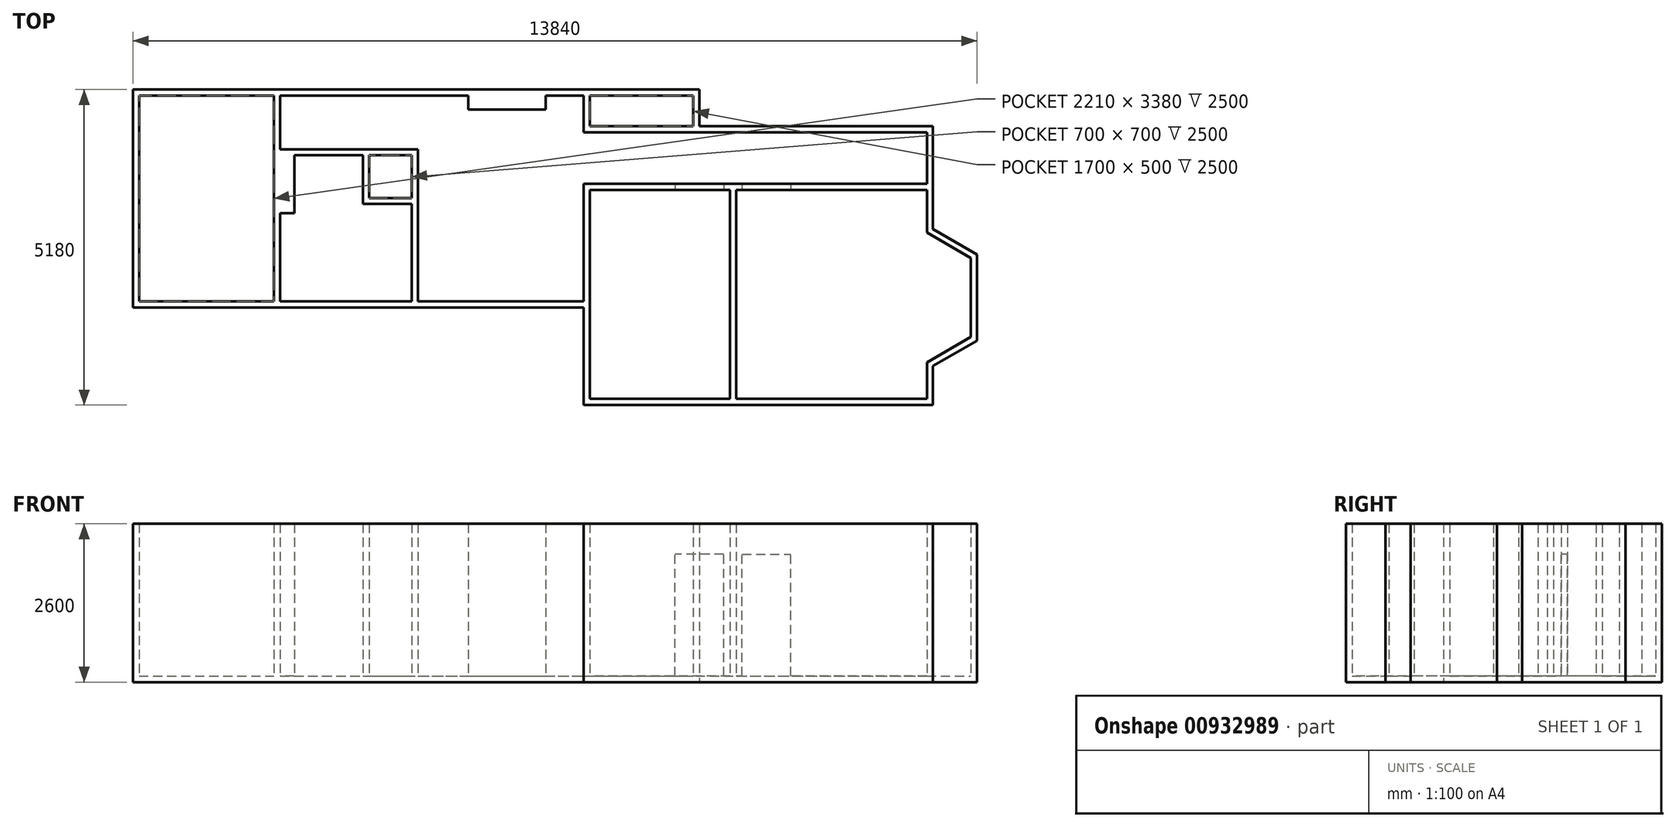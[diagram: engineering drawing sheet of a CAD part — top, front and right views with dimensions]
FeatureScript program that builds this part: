
annotation { "Feature Type Name" : "Feature", "Feature Type Description" : "" }
export const myFeature = defineFeature(function(context is Context, id is Id, definition is map)
    precondition{}
    {
        {
            var Q0;
            Q0=qCreatedBy(makeId("Top.planeOp"),FACE);
            var sketch = newSketch(context, id + "F0", { "sketchPlane" : qUnion([Q0])});
            skLineSegment(sketch, "E0", {"start": v(0, 0) * mm, "end": v(2210, 0) * mm});
            skLineSegment(sketch, "E1", {"start": v(0, 0) * mm, "end": v(0, -3380) * mm});
            skLineSegment(sketch, "E2", {"start": v(0, -3380) * mm, "end": v(2210, -3380) * mm});
            skLineSegment(sketch, "E3", {"start": v(7290, -600) * mm, "end": v(7290, 0) * mm});
            skLineSegment(sketch, "E4.0", {"start": v(-100, 100) * mm, "end": v(7390, 100) * mm});
            skLineSegment(sketch, "E4.1", {"start": v(-100, 100) * mm, "end": v(-100, -3480) * mm});
            skLineSegment(sketch, "E4.2", {"start": v(-100, -3480) * mm, "end": v(7290, -3480) * mm});
            skLineSegment(sketch, "E4.3", {"start": v(7390, -500) * mm, "end": v(7390, 0) * mm});
            skLineSegment(sketch, "E5", {"start": v(7290, 0) * mm, "end": v(7290, -600) * mm, "construction": true});
            skLineSegment(sketch, "E6", {"start": v(7390, -600) * mm, "end": v(11290, -600) * mm, "construction": true});
            skLineSegment(sketch, "E7", {"start": v(2210, -3380) * mm, "end": v(2210, 0) * mm});
            skLineSegment(sketch, "E8", {"start": v(2310, -3380) * mm, "end": v(2310, -1930) * mm});
            skLineSegment(sketch, "E9.trimOffspring", {"start": v(2310, 0) * mm, "end": v(5400, 0) * mm});
            skLineSegment(sketch, "E10.trimOffspring", {"start": v(2310, -3380) * mm, "end": v(4470, -3380) * mm});
            skLineSegment(sketch, "E11", {"start": v(2550, -980) * mm, "end": v(3670, -980) * mm});
            skLineSegment(sketch, "E12", {"start": v(4470, -1780) * mm, "end": v(4470, -3380) * mm});
            skLineSegment(sketch, "E13.0", {"start": v(4570, -880) * mm, "end": v(4570, -3380) * mm});
            skLineSegment(sketch, "E13.1", {"start": v(2310, -880) * mm, "end": v(4570, -880) * mm});
            skLineSegment(sketch, "E14.trimOffspring", {"start": v(2310, -880) * mm, "end": v(2310, 0) * mm});
            skLineSegment(sketch, "E15.trimOffspring", {"start": v(4570, -3380) * mm, "end": v(7290, -3380) * mm});
            skLineSegment(sketch, "E16", {"start": v(4570, 0) * mm, "end": v(5400, 0) * mm, "construction": true});
            skLineSegment(sketch, "E17", {"start": v(7290, 0) * mm, "end": v(6670, 0) * mm, "construction": true});
            skLineSegment(sketch, "E18", {"start": v(5400, 0) * mm, "end": v(5400, -230) * mm});
            skLineSegment(sketch, "E19", {"start": v(6670, -230) * mm, "end": v(6670, 0) * mm});
            skLineSegment(sketch, "E20", {"start": v(5400, -230) * mm, "end": v(6670, -230) * mm});
            skLineSegment(sketch, "E21.trimOffspring", {"start": v(6670, 0) * mm, "end": v(7290, 0) * mm});
            skLineSegment(sketch, "E22", {"start": v(3670, -980) * mm, "end": v(3670, -1780) * mm, "construction": true});
            skLineSegment(sketch, "E23", {"start": v(3670, -1780) * mm, "end": v(4470, -1780) * mm, "construction": true});
            skLineSegment(sketch, "E24.top", {"start": v(3670, -1780) * mm, "end": v(4470, -1780) * mm});
            skLineSegment(sketch, "E24.left", {"start": v(3670, -980) * mm, "end": v(3670, -1780) * mm});
            skLineSegment(sketch, "E25", {"start": v(2310, -3380) * mm, "end": v(2310, -1930) * mm, "construction": true});
            skLineSegment(sketch, "E26", {"start": v(3670, -980) * mm, "end": v(2550, -980) * mm});
            skLineSegment(sketch, "E27", {"start": v(2550, -980) * mm, "end": v(2550, -1930) * mm});
            skLineSegment(sketch, "E28", {"start": v(2550, -1930) * mm, "end": v(2310, -1930) * mm});
            skLineSegment(sketch, "E29", {"start": v(7390, -3480) * mm, "end": v(7390, -1550) * mm});
            skLineSegment(sketch, "E30", {"start": v(7390, -1450) * mm, "end": v(12620, -1450) * mm});
            skLineSegment(sketch, "E31", {"start": v(7390, -600) * mm, "end": v(12620, -600) * mm});
            skLineSegment(sketch, "E32.0", {"start": v(7390, -1550) * mm, "end": v(9690, -1550) * mm});
            skLineSegment(sketch, "E32.2", {"start": v(7390, -500) * mm, "end": v(9090, -500) * mm});
            skLineSegment(sketch, "E33", {"start": v(7390, -1550) * mm, "end": v(7390, -4980) * mm, "construction": true});
            skLineSegment(sketch, "E34.left", {"start": v(7390, -1550) * mm, "end": v(7390, -4980) * mm});
            skLineSegment(sketch, "E35.0", {"start": v(7290, -1550) * mm, "end": v(7290, -3380) * mm});
            skLineSegment(sketch, "E35.1", {"start": v(7290, -5080) * mm, "end": v(10190, -5080) * mm});
            skLineSegment(sketch, "E36.trimOffspring", {"start": v(7290, -3480) * mm, "end": v(7290, -5080) * mm});
            skLineSegment(sketch, "E37.trimOffspring", {"start": v(10190, -1550) * mm, "end": v(12720, -1550) * mm});
            skLineSegment(sketch, "E38", {"start": v(7390, -1450) * mm, "end": v(7290, -1450) * mm});
            skLineSegment(sketch, "E39", {"start": v(7290, -1450) * mm, "end": v(7290, -1550) * mm});
            skLineSegment(sketch, "E40", {"start": v(10190, -1550) * mm, "end": v(12920, -1550) * mm, "construction": true});
            skPoint(sketch, "E40.endSnap0", {"position": v(11455, -1550) * mm});
            skLineSegment(sketch, "E41.bottom", {"start": v(10190, -1550) * mm, "end": v(12920, -1550) * mm});
            skLineSegment(sketch, "E41.right", {"start": v(13640, -2665.7) * mm, "end": v(13640, -3964.3) * mm});
            skLineSegment(sketch, "E42.0", {"start": v(10190, -1450) * mm, "end": v(12920, -1450) * mm});
            skLineSegment(sketch, "E42.2", {"start": v(10190, -5080) * mm, "end": v(13020, -5080) * mm});
            skLineSegment(sketch, "E43", {"start": v(12920, -4980) * mm, "end": v(12920, -4380) * mm, "construction": true});
            skLineSegment(sketch, "E44", {"start": v(12920, -1550) * mm, "end": v(12920, -2250) * mm, "construction": true});
            skLineSegment(sketch, "E45", {"start": v(12920, -4980) * mm, "end": v(12920, -4380) * mm});
            skLineSegment(sketch, "E46", {"start": v(12920, -2250) * mm, "end": v(12920, -1550) * mm});
            skLineSegment(sketch, "E47", {"start": v(12920, -4980) * mm, "end": v(12210, -4980) * mm, "construction": true});
            skLineSegment(sketch, "E48.trimOffspring", {"start": v(12210, -4980) * mm, "end": v(12920, -4980) * mm});
            skLineSegment(sketch, "E49", {"start": v(12920, -2250) * mm, "end": v(13640, -2665.7) * mm});
            skLineSegment(sketch, "E50", {"start": v(12920, -4380) * mm, "end": v(13640, -3964.3) * mm});
            skPoint(sketch, "E51.start.orphan", {"position": v(13640, -4380) * mm});
            skPoint(sketch, "E52.orphan", {"position": v(13640, -1550) * mm});
            skLineSegment(sketch, "E53.0", {"start": v(13020, -2192.26) * mm, "end": v(13020, -1550) * mm});
            skLineSegment(sketch, "E53.1", {"start": v(13020, -4980) * mm, "end": v(13020, -4437.74) * mm});
            skLineSegment(sketch, "E53.2", {"start": v(13020, -4437.74) * mm, "end": v(13740, -4022.04) * mm});
            skLineSegment(sketch, "E53.3", {"start": v(13740, -2607.96) * mm, "end": v(13740, -4022.04) * mm});
            skLineSegment(sketch, "E53.4", {"start": v(13020, -2192.26) * mm, "end": v(13740, -2607.96) * mm});
            skLineSegment(sketch, "E54", {"start": v(12720, -500) * mm, "end": v(13020, -500) * mm});
            skLineSegment(sketch, "E55", {"start": v(13020, -500) * mm, "end": v(13020, -1550) * mm});
            skLineSegment(sketch, "E56", {"start": v(12620, -600) * mm, "end": v(12920, -600) * mm});
            skLineSegment(sketch, "E57", {"start": v(12920, -600) * mm, "end": v(12920, -1450) * mm});
            skLineSegment(sketch, "E58", {"start": v(13020, -4980) * mm, "end": v(13020, -5080) * mm});
            skLineSegment(sketch, "E59.trimOffspring", {"start": v(12210, -4980) * mm, "end": v(12920, -4980) * mm, "construction": true});
            skLineSegment(sketch, "E60", {"start": v(7290, -600) * mm, "end": v(7390, -600) * mm});
            skLineSegment(sketch, "E61", {"start": v(10190, -4980) * mm, "end": v(10890, -4980) * mm});
            skLineSegment(sketch, "E62.bottom", {"start": v(3770, -980) * mm, "end": v(4470, -980) * mm});
            skLineSegment(sketch, "E62.top", {"start": v(3770, -1680) * mm, "end": v(4470, -1680) * mm});
            skLineSegment(sketch, "E62.left", {"start": v(3770, -980) * mm, "end": v(3770, -1680) * mm});
            skLineSegment(sketch, "E62.right", {"start": v(4470, -980) * mm, "end": v(4470, -1680) * mm});
            skLineSegment(sketch, "E63", {"start": v(7390, -4980) * mm, "end": v(7890, -4980) * mm});
            skLineSegment(sketch, "E64", {"start": v(10090, -4980) * mm, "end": v(9790, -4980) * mm});
            skPoint(sketch, "E65.start.orphan", {"position": v(7890, -1550) * mm});
            skLineSegment(sketch, "E66.top", {"start": v(7390, 0) * mm, "end": v(9090, 0) * mm});
            skLineSegment(sketch, "E66.right", {"start": v(9090, -500) * mm, "end": v(9090, 0) * mm});
            skLineSegment(sketch, "E67", {"start": v(7390, 100) * mm, "end": v(9190, 100) * mm});
            skLineSegment(sketch, "E68", {"start": v(9190, 100) * mm, "end": v(9190, -500) * mm});
            skLineSegment(sketch, "E69.trimOffspring", {"start": v(9190, -500) * mm, "end": v(12720, -500) * mm});
            skLineSegment(sketch, "E70", {"start": v(10090, -1550) * mm, "end": v(9790, -1550) * mm});
            skLineSegment(sketch, "E71", {"start": v(9690, -1550) * mm, "end": v(9690, -4980) * mm});
            skLineSegment(sketch, "E72", {"start": v(9790, -1550) * mm, "end": v(9790, -4980) * mm});
            skLineSegment(sketch, "E73", {"start": v(10090, -1550) * mm, "end": v(10190, -1550) * mm});
            skLineSegment(sketch, "E74", {"start": v(10090, -4980) * mm, "end": v(10190, -4980) * mm});
            skLineSegment(sketch, "E75.trimOffspring", {"start": v(9690, -4980) * mm, "end": v(9590, -4980) * mm});
            skLineSegment(sketch, "E76", {"start": v(7890, -4980) * mm, "end": v(9590, -4980) * mm});
            skLineSegment(sketch, "E77", {"start": v(10890, -4980) * mm, "end": v(12210, -4980) * mm});
            skPoint(sketch, "E78.start.orphan", {"position": v(9590, -4500) * mm});
            skLineSegment(sketch, "E79.trimOffspring", {"start": v(9790, -1550) * mm, "end": v(10090, -1550) * mm});
            skSolve(sketch);
        }
        {
            var Q0;
            Q0=qSketchRegion(id+"F0",true);
            extrude(context, id + "F1", {"entities" : qUnion([Q0]), "depth" : 2500 * mm, "offsetDistance" : 25 * mm});
        }
        {
            var Q0;
            Q0=makeQuery(id+"F1.opExtrude","CAP_FACE",FACE,{"disambiguationData":[OSD([sQuery(id+"F0.wireOp",EDGE,"E0"),sQuery(id+"F0.wireOp",EDGE,"E1"),sQuery(id+"F0.wireOp",EDGE,"E2"),sQuery(id+"F0.wireOp",EDGE,"E3"),sQuery(id+"F0.wireOp",EDGE,"E4.0"),sQuery(id+"F0.wireOp",EDGE,"E4.1"),sQuery(id+"F0.wireOp",EDGE,"E4.2"),sQuery(id+"F0.wireOp",EDGE,"E7"),sQuery(id+"F0.wireOp",EDGE,"E8"),sQuery(id+"F0.wireOp",EDGE,"E9.trimOffspring"),sQuery(id+"F0.wireOp",EDGE,"E10.trimOffspring"),sQuery(id+"F0.wireOp",EDGE,"E12"),sQuery(id+"F0.wireOp",EDGE,"E13.0"),sQuery(id+"F0.wireOp",EDGE,"E13.1"),sQuery(id+"F0.wireOp",EDGE,"E14.trimOffspring"),sQuery(id+"F0.wireOp",EDGE,"E15.trimOffspring"),sQuery(id+"F0.wireOp",EDGE,"E18"),sQuery(id+"F0.wireOp",EDGE,"E19"),sQuery(id+"F0.wireOp",EDGE,"E20"),sQuery(id+"F0.wireOp",EDGE,"E21.trimOffspring"),sQuery(id+"F0.wireOp",EDGE,"E24.top"),sQuery(id+"F0.wireOp",EDGE,"E24.left"),sQuery(id+"F0.wireOp",EDGE,"E26"),sQuery(id+"F0.wireOp",EDGE,"E27"),sQuery(id+"F0.wireOp",EDGE,"E28"),sQuery(id+"F0.wireOp",EDGE,"E30"),sQuery(id+"F0.wireOp",EDGE,"E31"),sQuery(id+"F0.wireOp",EDGE,"E32.0"),sQuery(id+"F0.wireOp",EDGE,"E34.left"),sQuery(id+"F0.wireOp",EDGE,"E34.right"),sQuery(id+"F0.wireOp",EDGE,"E35.0"),sQuery(id+"F0.wireOp",EDGE,"E35.1"),sQuery(id+"F0.wireOp",EDGE,"E36.trimOffspring"),sQuery(id+"F0.wireOp",EDGE,"E38"),sQuery(id+"F0.wireOp",EDGE,"E39"),sQuery(id+"F0.wireOp",EDGE,"E41.bottom"),sQuery(id+"F0.wireOp",EDGE,"E41.left"),sQuery(id+"F0.wireOp",EDGE,"E41.right"),sQuery(id+"F0.wireOp",EDGE,"E42.0"),sQuery(id+"F0.wireOp",EDGE,"E42.2"),sQuery(id+"F0.wireOp",EDGE,"E45"),sQuery(id+"F0.wireOp",EDGE,"E46"),sQuery(id+"F0.wireOp",EDGE,"85VIIPWN-8tm0-qgK9-NPj0-ckiwgT15VhqN.top"),sQuery(id+"F0.wireOp",EDGE,"85VIIPWN-8tm0-qgK9-NPj0-ckiwgT15VhqN.left"),sQuery(id+"F0.wireOp",EDGE,"85VIIPWN-8tm0-qgK9-NPj0-ckiwgT15VhqN.right"),sQuery(id+"F0.wireOp",EDGE,"E48.trimOffspring"),sQuery(id+"F0.wireOp",EDGE,"E49"),sQuery(id+"F0.wireOp",EDGE,"E50"),sQuery(id+"F0.wireOp",EDGE,"E53.0"),sQuery(id+"F0.wireOp",EDGE,"E53.1"),sQuery(id+"F0.wireOp",EDGE,"E53.2"),sQuery(id+"F0.wireOp",EDGE,"E53.3"),sQuery(id+"F0.wireOp",EDGE,"E53.4"),sQuery(id+"F0.wireOp",EDGE,"E54"),sQuery(id+"F0.wireOp",EDGE,"E55"),sQuery(id+"F0.wireOp",EDGE,"E56"),sQuery(id+"F0.wireOp",EDGE,"E57"),sQuery(id+"F0.wireOp",EDGE,"E58"),sQuery(id+"F0.wireOp",EDGE,"E60"),sQuery(id+"F0.wireOp",EDGE,"E61"),sQuery(id+"F0.wireOp",EDGE,"E62.bottom"),sQuery(id+"F0.wireOp",EDGE,"E62.top"),sQuery(id+"F0.wireOp",EDGE,"E62.left"),sQuery(id+"F0.wireOp",EDGE,"E62.right"),sQuery(id+"F0.wireOp",EDGE,"E63"),sQuery(id+"F0.wireOp",EDGE,"E64"),sQuery(id+"F0.wireOp",EDGE,"IbvzqP4D-xqoy-G7iJ-oLV8-X3IewTjYSucs"),sQuery(id+"F0.wireOp",EDGE,"E78"),sQuery(id+"F0.wireOp",EDGE,"xuDYRinL-DUjp-Y6Bj-M5l4-YW6vaS1A13u5"),sQuery(id+"F0.wireOp",EDGE,"E32.2"),sQuery(id+"F0.wireOp",EDGE,"E66.top"),sQuery(id+"F0.wireOp",EDGE,"E4.3"),sQuery(id+"F0.wireOp",EDGE,"E66.right"),sQuery(id+"F0.wireOp",EDGE,"E67"),sQuery(id+"F0.wireOp",EDGE,"E68"),sQuery(id+"F0.wireOp",EDGE,"E69.trimOffspring")])],"isStart":true});
            var sketch = newSketch(context, id + "F2", { "sketchPlane" : qUnion([Q0])});
            skLineSegment(sketch, "E80.0", {"start": v(-100, 3480) * mm, "end": v(7290, 3480) * mm});
            skLineSegment(sketch, "E80.1", {"start": v(-100, -100) * mm, "end": v(9190, -100) * mm});
            skLineSegment(sketch, "E80.2", {"start": v(7290, 5080) * mm, "end": v(13020, 5080) * mm});
            skLineSegment(sketch, "E81.0", {"start": v(7290, 3480) * mm, "end": v(7290, 5080) * mm});
            skLineSegment(sketch, "E81.1", {"start": v(9190, -100) * mm, "end": v(9190, 500) * mm});
            skLineSegment(sketch, "E82.0", {"start": v(9190, 500) * mm, "end": v(13020, 500) * mm});
            skLineSegment(sketch, "E83.0", {"start": v(13020, 2192.26) * mm, "end": v(13020, 500) * mm});
            skLineSegment(sketch, "E84.0", {"start": v(13020, 2192.26) * mm, "end": v(13740, 2607.96) * mm});
            skLineSegment(sketch, "E85.0", {"start": v(13740, 2607.96) * mm, "end": v(13740, 4022.04) * mm});
            skLineSegment(sketch, "E86.0", {"start": v(13020, 4437.74) * mm, "end": v(13740, 4022.04) * mm});
            skLineSegment(sketch, "E87.0", {"start": v(13020, 4437.74) * mm, "end": v(13020, 5080) * mm});
            skLineSegment(sketch, "E88", {"start": v(13740, 2607.96) * mm, "end": v(13020, 2192.26) * mm});
            skLineSegment(sketch, "E89", {"start": v(13020, 500) * mm, "end": v(9190, 500) * mm});
            skLineSegment(sketch, "E90", {"start": v(9190, -100) * mm, "end": v(-100, -100) * mm});
            skLineSegment(sketch, "E91", {"start": v(-100, 3480) * mm, "end": v(-100, -100) * mm});
            skSolve(sketch);
        }
        {
            var Q0;
            Q0=qSketchRegion(id+"F2",true);
            extrude(context, id + "F3", {"entities" : qUnion([Q0]), "operationType" : NewBodyOperationType.ADD, "depth" : 100 * mm, "offsetDistance" : 25 * mm});
        }
        {
            var Q0;
            Q0=makeQuery(id+"F1.opExtrude","SWEPT_FACE",FACE,{"disambiguationData":[OSD([sQuery(id+"F0.wireOp",EDGE,"E41.bottom"),sQuery(id+"F0.wireOp",EDGE,"E73"),sQuery(id+"F0.wireOp",EDGE,"E79.trimOffspring")])]});
            var sketch = newSketch(context, id + "F4", { "sketchPlane" : qUnion([Q0])});
            skLineSegment(sketch, "E92", {"start": v(9790, 0) * mm, "end": v(9890, 0) * mm, "construction": true});
            skLineSegment(sketch, "E93.bottom", {"start": v(9890, 0) * mm, "end": v(10690, 0) * mm});
            skLineSegment(sketch, "E93.top", {"start": v(9890, 2000) * mm, "end": v(10690, 2000) * mm});
            skLineSegment(sketch, "E93.left", {"start": v(9890, 0) * mm, "end": v(9890, 2000) * mm});
            skLineSegment(sketch, "E93.right", {"start": v(10690, 0) * mm, "end": v(10690, 2000) * mm});
            skLineSegment(sketch, "E94", {"start": v(9790, 0) * mm, "end": v(9590, 0) * mm, "construction": true});
            skLineSegment(sketch, "E95.bottom", {"start": v(9590, 0) * mm, "end": v(8790, 0) * mm});
            skLineSegment(sketch, "E95.top", {"start": v(9590, 2000) * mm, "end": v(8790, 2000) * mm});
            skLineSegment(sketch, "E95.left", {"start": v(9590, 0) * mm, "end": v(9590, 2000) * mm});
            skLineSegment(sketch, "E95.right", {"start": v(8790, 0) * mm, "end": v(8790, 2000) * mm});
            skSolve(sketch);
        }
        {
            var Q0;
            Q0 = qSketchRegion(id + "F4", true);
            extrude(context, id + "F5", {"entities" : qUnion([Q0]), "operationType" : NewBodyOperationType.REMOVE, "endBound" : BoundingType.UP_TO_NEXT, "oppositeDirection" : true, "depth" : 25 * mm, "offsetDistance" : 25 * mm});
        }
    });
